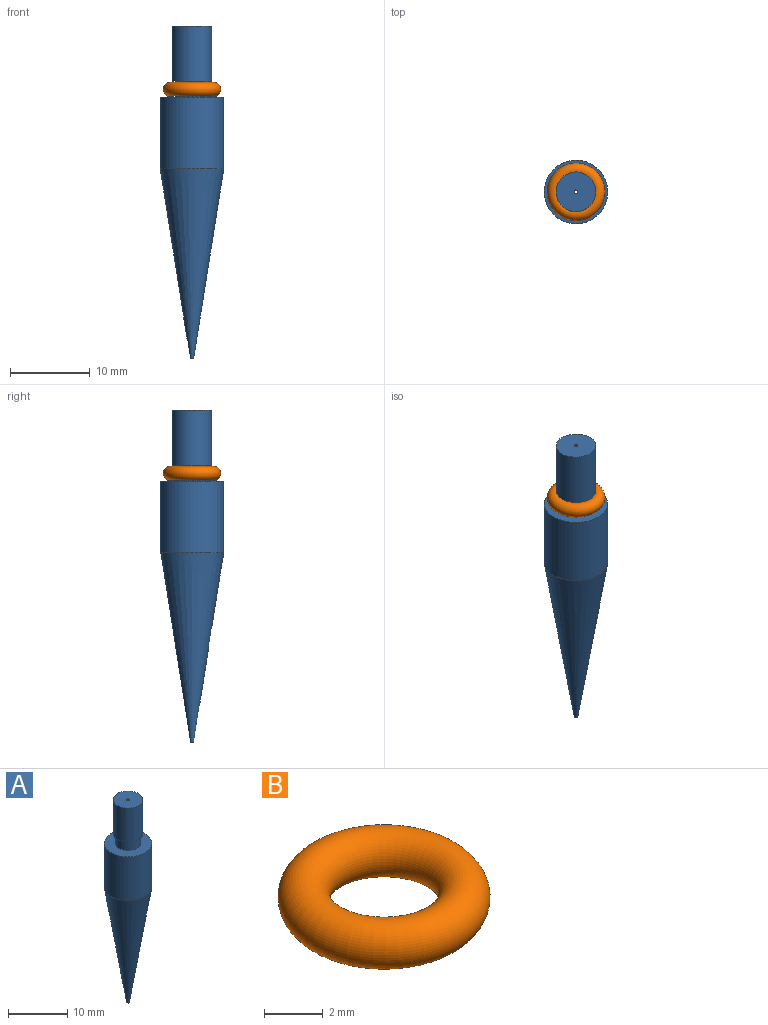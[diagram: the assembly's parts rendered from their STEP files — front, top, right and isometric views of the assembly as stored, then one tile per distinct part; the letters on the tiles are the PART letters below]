
ASSEMBLY  parts=2 mates=1
PART A: 8 faces, bbox 8x8x41.8 mm
  f0: plane 5x5mm, normal (0,0,1), area 19.5mm2, adj f6,f7
  f1: cone r=3.99mm half-angle=9deg, axis (0,0,1), area 319.3mm2, adj f2,f7
  f2: cylinder r=3.99mm len=8.99mm, axis (0,0,1), area 225.7mm2, adj f1,f3
  f3: plane 7.99x7.99mm, normal (0,0,1), area 35.8mm2, adj f2,f4
  f4: cylinder r=2.14mm len=4.27mm, axis (0,0,1), area 27.3mm2, adj f3,f5
  f5: plane 5x5mm, normal (0,0,-1), area 5.3mm2, adj f4,f6
  f6: cylinder r=2.5mm len=6.96mm, axis (0,0,1), area 109.3mm2, adj f0,f5
  f7: cylinder r=0.23mm len=41.76mm, axis (0,0,1), area 60mm2, adj f0,f1
PART B: 1 faces, bbox 7.8x7.8x1.8 mm
  f0: torus R=2.73mm, axis (0,0,1), area 95.8mm2
PLACE A t=(0.62,-9.51,1.98)mm
PLACE B t=(0.62,-9.51,-5.99)mm
MATE fastened B.f0 <-> A.f1  axis (0,0,1) through (0.62,-9.51,-5.99)mm
